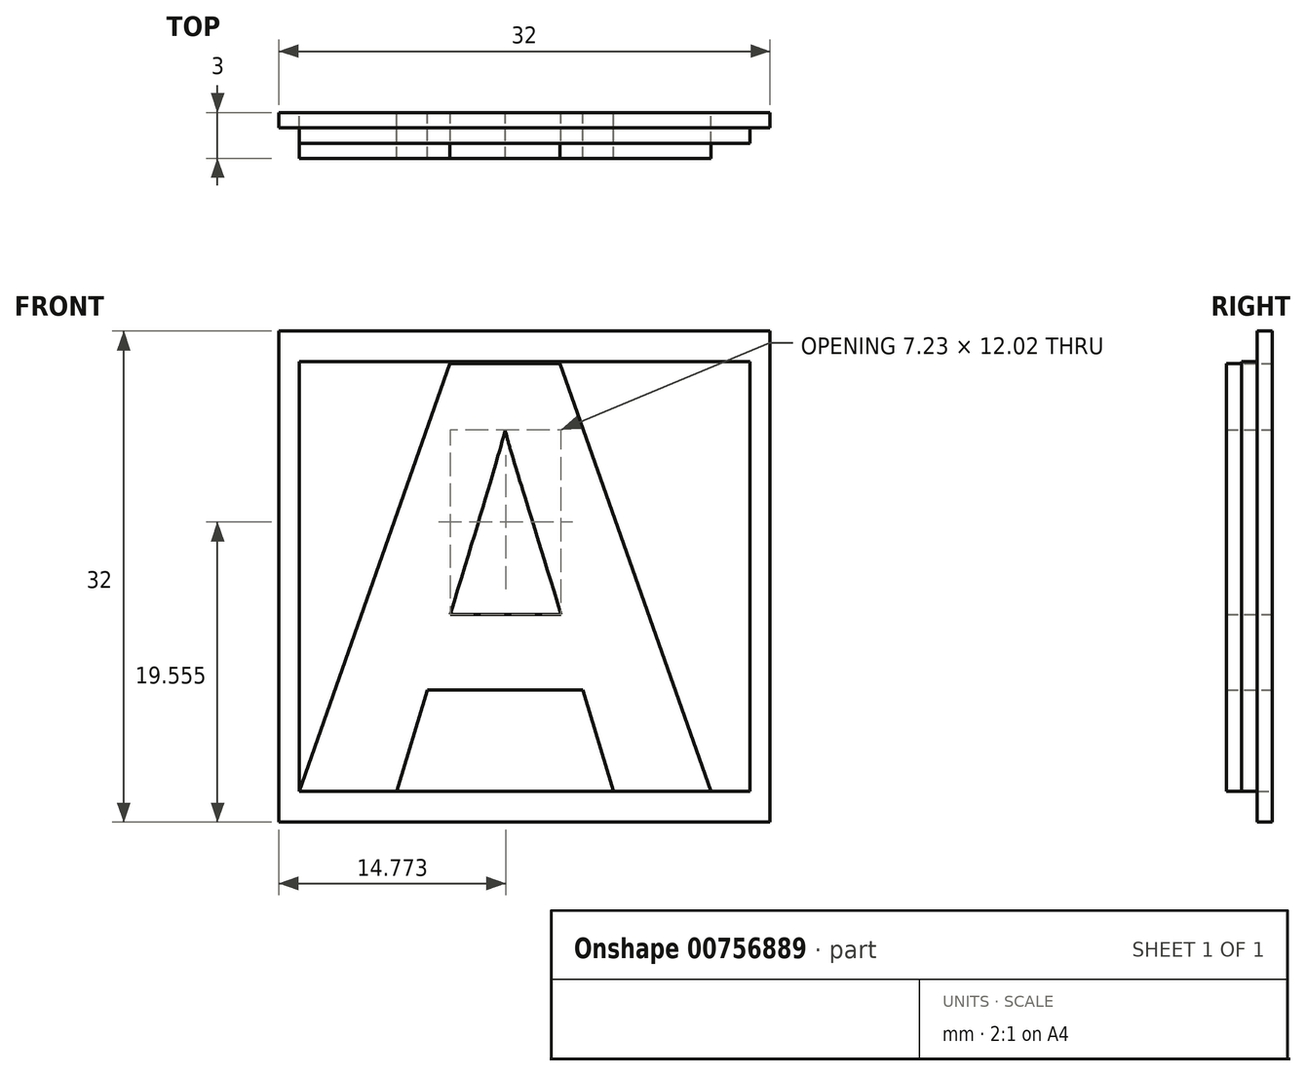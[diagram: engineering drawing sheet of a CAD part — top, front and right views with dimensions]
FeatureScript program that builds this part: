
annotation { "Feature Type Name" : "Feature", "Feature Type Description" : "" }
export const myFeature = defineFeature(function(context is Context, id is Id, definition is map)
    precondition{}
    {
        {
            var Q0;
            Q0=qCreatedBy(makeId("Front.planeOp"),FACE);
            var sketch = newSketch(context, id + "F0", { "sketchPlane" : qUnion([Q0])});
            skLineSegment(sketch, "E0.bottom", {"start": v(16, -16) * mm, "end": v(-16, -16) * mm});
            skLineSegment(sketch, "E0.top", {"start": v(16, 16) * mm, "end": v(-16, 16) * mm});
            skLineSegment(sketch, "E0.left", {"start": v(16, -16) * mm, "end": v(16, 16) * mm});
            skLineSegment(sketch, "E0.right", {"start": v(-16, -16) * mm, "end": v(-16, 16) * mm});
            skPoint(sketch, "E0.middle", {"position": v(0, 0) * mm});
            skLineSegment(sketch, "E1.bottom", {"start": v(14.68, -14) * mm, "end": v(-14.68, -14) * mm});
            skLineSegment(sketch, "E1.top", {"start": v(14.68, 14) * mm, "end": v(-14.68, 14) * mm});
            skLineSegment(sketch, "E1.left", {"start": v(14.68, -14) * mm, "end": v(14.68, 14) * mm});
            skLineSegment(sketch, "E1.right", {"start": v(-14.68, -14) * mm, "end": v(-14.68, 14) * mm});
            skText(sketch, "E2", { "text": "A", "fontName": "OpenSans-Bold.ttf"});
            const initialGuessF0  = {"E2": [-0.01468, -0.014, 1, 0, 0.028]};
            skSetInitialGuess(sketch, initialGuessF0);
            skSolve(sketch);
        }
        {
            var Q0;
            Q0=makeQuery(id+"F0.imprint","IMPRINT",FACE,{"disambiguationData":[TD([[makeQuery(id+"F0.imprint","IMPRINT",EDGE,{"derivedFrom":sQuery(id+"F0.wireOp",EDGE,"E0.bottom")}),-1.0]])]});
            extrude(context, id + "F1", {"entities" : qUnion([Q0]), "depth" : 1 * mm, "offsetDistance" : 25 * mm});
        }
        {
            var Q0;
            Q0=makeQuery(id+"F0.imprint","IMPRINT",FACE,{"disambiguationData":[TD([[makeQuery(id+"F0.imprint","IMPRINT",EDGE,{"derivedFrom":sQuery(id+"F0.wireOp",EDGE,"E1.top")}),1.0]])]});
            var Q1;
            Q1=makeQuery(id+"F0.imprint","IMPRINT",FACE,{"disambiguationData":[TD([[makeQuery(id+"F0.imprint","IMPRINT",EDGE,{"derivedFrom":sQuery(id+"F0.wireOp",EDGE,"E2.sketch_text.stroke-8")}),1.0]])]});
            var Q2;
            {var subQ2=sQuery(id+"F0.wireOp",EDGE,"E2.sketch_text.stroke-0");Q2=makeQuery(id+"F0.imprint","IMPRINT",FACE,{"disambiguationData":[TD([[makeQuery(id+"F0.imprint","IMPRINT",EDGE,{"derivedFrom":subQ2}),1.0]])]});}
            extrude(context, id + "F2", {"entities" : qUnion([Q0, Q1, Q2]), "operationType" : NewBodyOperationType.ADD, "depth" : 2 * mm, "offsetDistance" : 25 * mm});
        }
        {
            var Q0;
            Q0=makeQuery(id+"F0.imprint","IMPRINT",FACE,{"disambiguationData":[TD([[makeQuery(id+"F0.imprint","IMPRINT",EDGE,{"derivedFrom":sQuery(id+"F0.wireOp",EDGE,"E2.sketch_text.stroke-0")}),-1.0]])]});
            extrude(context, id + "F3", {"entities" : qUnion([Q0]), "depth" : 3 * mm, "offsetDistance" : 25 * mm});
        }
    });
